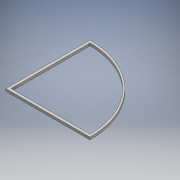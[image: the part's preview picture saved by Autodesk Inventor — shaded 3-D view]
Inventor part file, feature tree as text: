
AUTODESK INVENTOR PART (.ipt)
format: ipt  version: 2016 (Build 200138000, 138)  size: 131,072 bytes
history: native  units: mm
features: thread x4, extrude x3, sketch x3
ambient origin geometry x8: Origin, YZ Plane, XZ Plane, XY Plane, X Axis, Y Axis, Z Axis, Center Point
bodies: 实体1 (feature_tree)
feature tree (10):
  extrude  "拉伸1"  Depth=500.0mm
  extrude  "拉伸2"  Depth=15.0mm
  thread  "螺纹1"  [1 undecoded]
  thread  "螺纹2"  [1 undecoded]
  extrude  "拉伸3"  Depth=500.0mm
  thread  "螺纹3"  [1 undecoded]
  thread  "螺纹4"  [1 undecoded]
  sketch  "草图1"  dims[d0=500.0mm d1=500.0mm]
  sketch  "草图2"  dims[d2=15.0mm d3=15.0mm d4=470.0mm d5=470.0mm]
  sketch  "草图3"  dims[d6=470.0mm d7=500.0mm d8=15.0mm d9=0.0mm d10=5.0mm d11=5.0mm d12=30.0mm d13=430.0mm d14=430.0mm d15=0.0mm d16=10.0mm d17=0.0mm d18=10.0mm d19=0.0mm d20=7.5mm d21=7.5mm d22=5.0mm d23=5.0mm d24=30.0mm d25=430.0mm d26=7.5mm d27=7.5mm d28=5.0mm d29=0.0mm d30=10.0mm d31=0.0mm d32=10.0mm d33=0.0mm]
note: 4 required parameter values undecoded (feature->parameter linkage not recoverable at this tier; creation-order binding heuristic only, values carry confidence <= 0.55)
